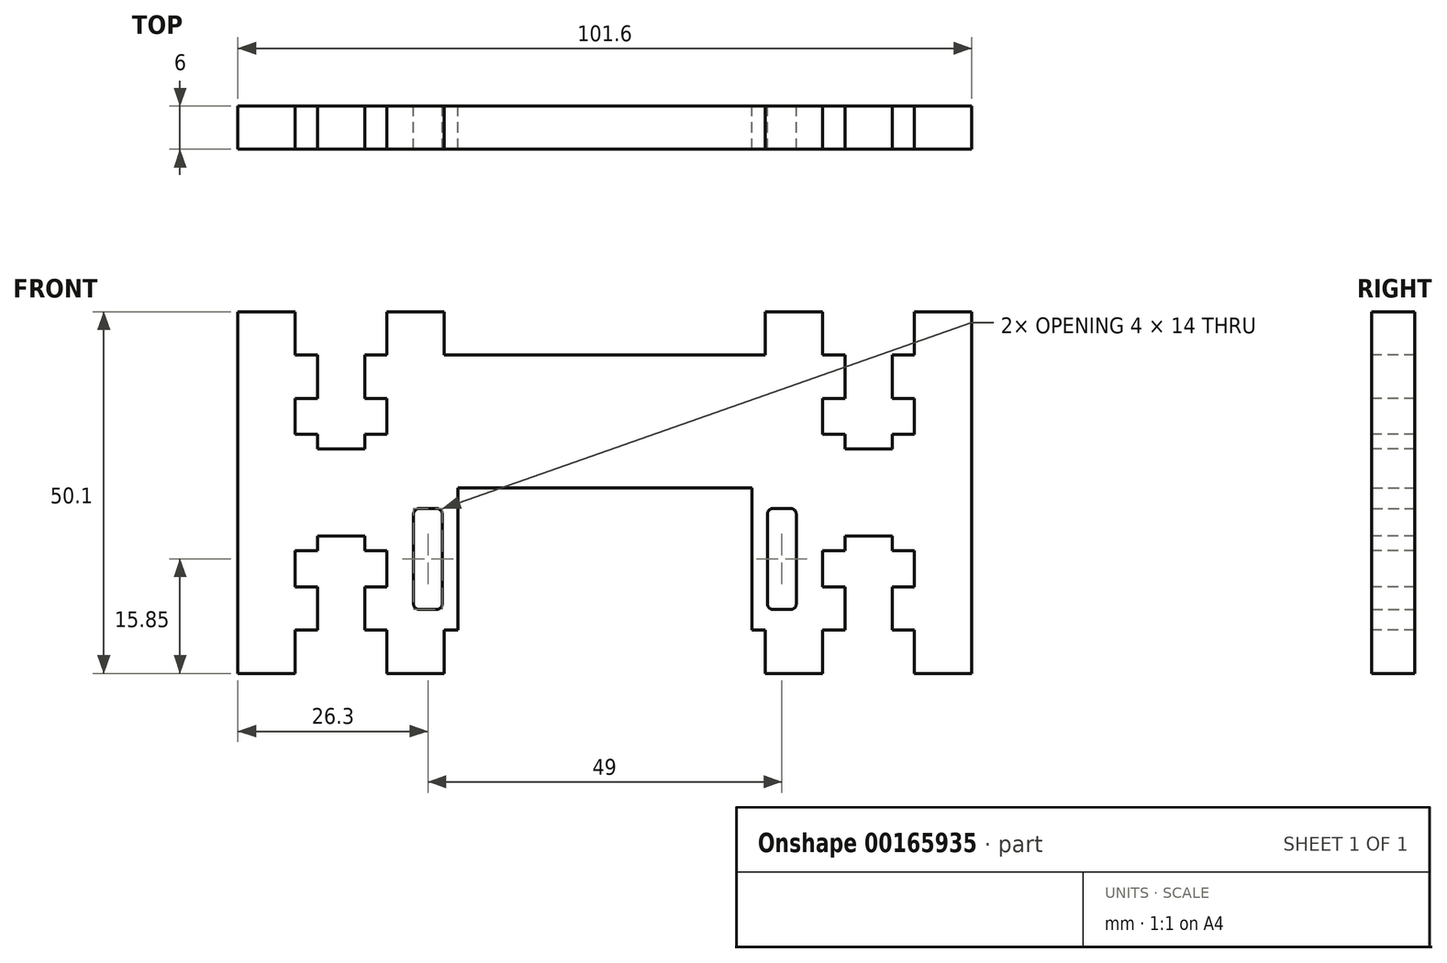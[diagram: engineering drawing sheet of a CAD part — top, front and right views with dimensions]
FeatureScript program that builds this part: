
annotation { "Feature Type Name" : "Feature", "Feature Type Description" : "" }
export const myFeature = defineFeature(function(context is Context, id is Id, definition is map)
    precondition{}
    {
        {
            var Q0;
            Q0=qCreatedBy(makeId("Front.planeOp"),FACE);
            var sketch = newSketch(context, id + "F0", { "sketchPlane" : qUnion([Q0])});
            skLineSegment(sketch, "E0.bottom", {"start": v(-50.8, 38.1) * mm, "end": v(50.8, 38.1) * mm});
            skLineSegment(sketch, "E0.top", {"start": v(-50.8, 0) * mm, "end": v(50.8, 0) * mm});
            skLineSegment(sketch, "E0.left", {"start": v(-50.8, 38.1) * mm, "end": v(-50.8, 0) * mm});
            skLineSegment(sketch, "E0.right", {"start": v(50.8, 38.1) * mm, "end": v(50.8, 0) * mm});
            skPoint(sketch, "E1", {"position": v(0, 0) * mm});
            skLineSegment(sketch, "E2.bottom", {"start": v(-20.35, 0) * mm, "end": v(20.35, 0) * mm});
            skLineSegment(sketch, "E2.top", {"start": v(-20.35, 19.7) * mm, "end": v(20.35, 19.7) * mm});
            skLineSegment(sketch, "E2.left", {"start": v(-20.35, 0) * mm, "end": v(-20.35, 19.7) * mm});
            skLineSegment(sketch, "E2.right", {"start": v(20.35, 0) * mm, "end": v(20.35, 19.7) * mm});
            skPoint(sketch, "E3", {"position": v(0, 19.7) * mm});
            skLineSegment(sketch, "E4.bottom", {"start": v(22.5, 16.85) * mm, "end": v(26.5, 16.85) * mm});
            skLineSegment(sketch, "E4.top", {"start": v(22.5, 2.85) * mm, "end": v(26.5, 2.85) * mm});
            skLineSegment(sketch, "E4.left", {"start": v(22.5, 16.85) * mm, "end": v(22.5, 2.85) * mm});
            skLineSegment(sketch, "E4.right", {"start": v(26.5, 16.85) * mm, "end": v(26.5, 2.85) * mm});
            skLineSegment(sketch, "E5", {"start": v(-20.35, 9.85) * mm, "end": v(36.92, 9.85) * mm, "construction": true});
            skPoint(sketch, "E6", {"position": v(26.5, 9.85) * mm});
            skLineSegment(sketch, "E7", {"start": v(24.5, 16.85) * mm, "end": v(24.5, 2.85) * mm, "construction": true});
            skLineSegment(sketch, "E8.MirrorCS", {"start": v(-22.5, 16.85) * mm, "end": v(-22.5, 2.85) * mm});
            skLineSegment(sketch, "E9.MirrorCS", {"start": v(-26.5, 16.85) * mm, "end": v(-26.5, 2.85) * mm});
            skLineSegment(sketch, "E10.MirrorCS", {"start": v(-22.5, 16.85) * mm, "end": v(-26.5, 16.85) * mm});
            skLineSegment(sketch, "E11.MirrorCS", {"start": v(-22.5, 2.85) * mm, "end": v(-26.5, 2.85) * mm});
            skSolve(sketch);
        }
        {
            var Q0;
            Q0=makeQuery(id+"F0.imprint","IMPRINT",FACE,{"disambiguationData":[TD([[makeQuery(id+"F0.imprint","IMPRINT",EDGE,{"derivedFrom":sQuery(id+"F0.wireOp",EDGE,"E0.bottom")}),-1.0]])]});
            extrude(context, id + "F1", {"entities" : qUnion([Q0]), "depth" : 6 * mm});
        }
        {
            var Q0;
            Q0=makeQuery(id+"F1.opExtrude","SWEPT_EDGE",EDGE,{"disambiguationData":[OSD([sQuery(id+"F0.wireOp",EDGE,"E9.MirrorCS"),sQuery(id+"F0.wireOp",EDGE,"E10.MirrorCS")])]});
            var Q1;
            Q1=makeQuery(id+"F1.opExtrude","SWEPT_EDGE",EDGE,{"disambiguationData":[OSD([sQuery(id+"F0.wireOp",EDGE,"E8.MirrorCS"),sQuery(id+"F0.wireOp",EDGE,"E11.MirrorCS")])]});
            var Q2;
            Q2=makeQuery(id+"F1.opExtrude","SWEPT_EDGE",EDGE,{"disambiguationData":[OSD([sQuery(id+"F0.wireOp",EDGE,"E8.MirrorCS"),sQuery(id+"F0.wireOp",EDGE,"E10.MirrorCS")])]});
            var Q3;
            Q3=makeQuery(id+"F1.opExtrude","SWEPT_EDGE",EDGE,{"disambiguationData":[OSD([sQuery(id+"F0.wireOp",EDGE,"E9.MirrorCS"),sQuery(id+"F0.wireOp",EDGE,"E11.MirrorCS")])]});
            var Q4;
            Q4=makeQuery(id+"F1.opExtrude","SWEPT_EDGE",EDGE,{"disambiguationData":[OSD([sQuery(id+"F0.wireOp",EDGE,"E4.top"),sQuery(id+"F0.wireOp",EDGE,"E4.left")])]});
            var Q5;
            Q5=makeQuery(id+"F1.opExtrude","SWEPT_EDGE",EDGE,{"disambiguationData":[OSD([sQuery(id+"F0.wireOp",EDGE,"E4.bottom"),sQuery(id+"F0.wireOp",EDGE,"E4.left")])]});
            var Q6;
            Q6=makeQuery(id+"F1.opExtrude","SWEPT_EDGE",EDGE,{"disambiguationData":[OSD([sQuery(id+"F0.wireOp",EDGE,"E4.bottom"),sQuery(id+"F0.wireOp",EDGE,"E4.right")])]});
            var Q7;
            Q7=makeQuery(id+"F1.opExtrude","SWEPT_EDGE",EDGE,{"disambiguationData":[OSD([sQuery(id+"F0.wireOp",EDGE,"E4.top"),sQuery(id+"F0.wireOp",EDGE,"E4.right")])]});
            fillet(context, id + "F2", {"entities" : qUnion([Q0, Q1, Q2, Q3, Q4, Q5, Q6, Q7]), "radius" : .8 * mm, "tangentPropagation" : true, "allowEdgeOverflow" : false});
        }
        {
            var Q0;
            {var subQ0=sQuery(id+"F0.wireOp",EDGE,"E0.top");Q0=makeQuery(id+"F1.opExtrude","SWEPT_FACE",FACE,{"disambiguationData":[OSD([subQ0]),TDD([makeQuery(id+"F0.imprint","IMPRINT",EDGE,{"disambiguationData":[TD([[makeQuery(id+"F0.imprint","INTERSECT",VERTEX,{"derivedFrom":[subQ0,sQuery(id+"F0.wireOp",EDGE,"E0.left")]}),-1.0]])],"derivedFrom":subQ0})])]});}
            var sketch = newSketch(context, id + "F3", { "sketchPlane" : qUnion([Q0])});
            skLineSegment(sketch, "E12.bottom", {"start": v(-50.8, 6) * mm, "end": v(-42.86, 6) * mm});
            skLineSegment(sketch, "E12.top", {"start": v(-50.8, 0) * mm, "end": v(-42.86, 0) * mm});
            skLineSegment(sketch, "E12.left", {"start": v(-50.8, 6) * mm, "end": v(-50.8, 0) * mm});
            skLineSegment(sketch, "E12.right", {"start": v(-42.86, 6) * mm, "end": v(-42.86, 0) * mm});
            skLineSegment(sketch, "E13.MirrorCS", {"start": v(50.8, 0) * mm, "end": v(42.86, 0) * mm});
            skLineSegment(sketch, "E14.MirrorCS", {"start": v(42.86, 6) * mm, "end": v(42.86, 0) * mm});
            skLineSegment(sketch, "E15.MirrorCS", {"start": v(50.8, 6) * mm, "end": v(42.86, 6) * mm});
            skLineSegment(sketch, "E16.MirrorCS", {"start": v(50.8, 6) * mm, "end": v(50.8, 0) * mm});
            skLineSegment(sketch, "E17.bottom", {"start": v(-30.16, 6) * mm, "end": v(-22.23, 6) * mm});
            skLineSegment(sketch, "E17.top", {"start": v(-30.16, 0) * mm, "end": v(-22.23, 0) * mm});
            skLineSegment(sketch, "E17.left", {"start": v(-30.16, 6) * mm, "end": v(-30.16, 0) * mm});
            skLineSegment(sketch, "E17.right", {"start": v(-22.23, 6) * mm, "end": v(-22.23, 0) * mm});
            skLineSegment(sketch, "E18.bottom", {"start": v(30.16, 6) * mm, "end": v(22.23, 6) * mm});
            skLineSegment(sketch, "E18.top", {"start": v(30.16, 0) * mm, "end": v(22.23, 0) * mm});
            skLineSegment(sketch, "E18.left", {"start": v(30.16, 6) * mm, "end": v(30.16, 0) * mm});
            skLineSegment(sketch, "E18.right", {"start": v(22.23, 6) * mm, "end": v(22.23, 0) * mm});
            skSolve(sketch);
        }
        {
            var Q0;
            Q0=qSketchRegion(id+"F3",true);
            extrude(context, id + "F4", {"entities" : qUnion([Q0]), "operationType" : NewBodyOperationType.ADD, "depth" : 6 * mm});
        }
        {
            var Q0;
            Q0=makeQuery(id+"F1.opExtrude","SWEPT_FACE",FACE,{"disambiguationData":[OSD([sQuery(id+"F0.wireOp",EDGE,"E0.bottom")])]});
            var sketch = newSketch(context, id + "F5", { "sketchPlane" : qUnion([Q0])});
            skLineSegment(sketch, "E19.bottom", {"start": v(-50.8, 0) * mm, "end": v(-42.86, 0) * mm});
            skLineSegment(sketch, "E19.top", {"start": v(-50.8, -6) * mm, "end": v(-42.86, -6) * mm});
            skLineSegment(sketch, "E19.left", {"start": v(-50.8, 0) * mm, "end": v(-50.8, -6) * mm});
            skLineSegment(sketch, "E19.right", {"start": v(-42.86, 0) * mm, "end": v(-42.86, -6) * mm});
            skLineSegment(sketch, "E20.bottom", {"start": v(-30.16, 0) * mm, "end": v(-22.22, 0) * mm});
            skLineSegment(sketch, "E20.top", {"start": v(-30.16, -6) * mm, "end": v(-22.22, -6) * mm});
            skLineSegment(sketch, "E20.left", {"start": v(-30.16, 0) * mm, "end": v(-30.16, -6) * mm});
            skLineSegment(sketch, "E20.right", {"start": v(-22.22, 0) * mm, "end": v(-22.22, -6) * mm});
            skLineSegment(sketch, "E21.bottom", {"start": v(22.23, 0) * mm, "end": v(30.16, 0) * mm});
            skLineSegment(sketch, "E21.top", {"start": v(22.23, -6) * mm, "end": v(30.16, -6) * mm});
            skLineSegment(sketch, "E21.left", {"start": v(22.23, 0) * mm, "end": v(22.23, -6) * mm});
            skLineSegment(sketch, "E21.right", {"start": v(30.16, 0) * mm, "end": v(30.16, -6) * mm});
            skLineSegment(sketch, "E22.bottom", {"start": v(42.86, 0) * mm, "end": v(50.8, 0) * mm});
            skLineSegment(sketch, "E22.top", {"start": v(42.86, -6) * mm, "end": v(50.8, -6) * mm});
            skLineSegment(sketch, "E22.left", {"start": v(42.86, 0) * mm, "end": v(42.86, -6) * mm});
            skLineSegment(sketch, "E22.right", {"start": v(50.8, 0) * mm, "end": v(50.8, -6) * mm});
            skSolve(sketch);
        }
        {
            var Q0;
            Q0=qSketchRegion(id+"F5",true);
            extrude(context, id + "F6", {"entities" : qUnion([Q0]), "operationType" : NewBodyOperationType.ADD, "depth" : 6 * mm});
        }
        {
            var Q0;
            Q0=makeQuery(id+"F6.boolean.opBoolean","MERGE",FACE,{"derivedFrom":[makeQuery(id+"F4.boolean.opBoolean","MERGE",FACE,{"derivedFrom":[makeQuery(id+"F1.opExtrude","CAP_FACE",FACE,{"disambiguationData":[OSD([sQuery(id+"F0.wireOp",EDGE,"E0.bottom"),sQuery(id+"F0.wireOp",EDGE,"E0.top"),sQuery(id+"F0.wireOp",EDGE,"E0.left"),sQuery(id+"F0.wireOp",EDGE,"E0.right"),sQuery(id+"F0.wireOp",EDGE,"E2.top"),sQuery(id+"F0.wireOp",EDGE,"E2.left"),sQuery(id+"F0.wireOp",EDGE,"E2.right"),sQuery(id+"F0.wireOp",EDGE,"E4.bottom"),sQuery(id+"F0.wireOp",EDGE,"E4.top"),sQuery(id+"F0.wireOp",EDGE,"E4.left"),sQuery(id+"F0.wireOp",EDGE,"E4.right"),sQuery(id+"F0.wireOp",EDGE,"E8.MirrorCS"),sQuery(id+"F0.wireOp",EDGE,"E9.MirrorCS"),sQuery(id+"F0.wireOp",EDGE,"E10.MirrorCS"),sQuery(id+"F0.wireOp",EDGE,"E11.MirrorCS")])],"isStart":false}),makeQuery(id+"F4.opExtrude","SWEPT_FACE",FACE,{"disambiguationData":[OSD([sQuery(id+"F3.wireOp",EDGE,"E12.bottom")])]}),makeQuery(id+"F4.opExtrude","SWEPT_FACE",FACE,{"disambiguationData":[OSD([sQuery(id+"F3.wireOp",EDGE,"E15.MirrorCS")])]}),makeQuery(id+"F4.opExtrude","SWEPT_FACE",FACE,{"disambiguationData":[OSD([sQuery(id+"F3.wireOp",EDGE,"E17.bottom")])]}),makeQuery(id+"F4.opExtrude","SWEPT_FACE",FACE,{"disambiguationData":[OSD([sQuery(id+"F3.wireOp",EDGE,"E18.bottom")])]})]}),makeQuery(id+"F6.opExtrude","SWEPT_FACE",FACE,{"disambiguationData":[OSD([sQuery(id+"F5.wireOp",EDGE,"E19.top")])]}),makeQuery(id+"F6.opExtrude","SWEPT_FACE",FACE,{"disambiguationData":[OSD([sQuery(id+"F5.wireOp",EDGE,"E20.top")])]}),makeQuery(id+"F6.opExtrude","SWEPT_FACE",FACE,{"disambiguationData":[OSD([sQuery(id+"F5.wireOp",EDGE,"E21.top")])]}),makeQuery(id+"F6.opExtrude","SWEPT_FACE",FACE,{"disambiguationData":[OSD([sQuery(id+"F5.wireOp",EDGE,"E22.top")])]})]});
            var sketch = newSketch(context, id + "F7", { "sketchPlane" : qUnion([Q0])});
            skLineSegment(sketch, "E23", {"start": v(0, 38.1) * mm, "end": v(0, 19.7) * mm, "construction": true});
            skLineSegment(sketch, "E24", {"start": v(-50.8, 19.05) * mm, "end": v(50.8, 19.05) * mm, "construction": true});
            skLineSegment(sketch, "E25", {"start": v(-36.51, 38.1) * mm, "end": v(-39.76, 38.1) * mm});
            skLineSegment(sketch, "E26", {"start": v(-39.76, 38.1) * mm, "end": v(-39.76, 32.1) * mm});
            skLineSegment(sketch, "E27", {"start": v(-39.76, 32.1) * mm, "end": v(-42.86, 32.1) * mm});
            skLineSegment(sketch, "E28", {"start": v(-42.86, 32.1) * mm, "end": v(-42.86, 27.1) * mm});
            skLineSegment(sketch, "E29", {"start": v(-42.86, 27.1) * mm, "end": v(-39.76, 27.1) * mm});
            skLineSegment(sketch, "E30", {"start": v(-39.76, 27.1) * mm, "end": v(-39.76, 25.1) * mm});
            skLineSegment(sketch, "E31", {"start": v(-39.76, 25.1) * mm, "end": v(-36.51, 25.1) * mm});
            skLineSegment(sketch, "E32", {"start": v(-36.51, 38.1) * mm, "end": v(-36.51, 25.1) * mm, "construction": true});
            skLineSegment(sketch, "E33.MirrorCS", {"start": v(-36.51, 38.1) * mm, "end": v(-33.26, 38.1) * mm});
            skLineSegment(sketch, "E34.MirrorCS", {"start": v(-33.26, 38.1) * mm, "end": v(-33.26, 32.1) * mm});
            skLineSegment(sketch, "E35.MirrorCS", {"start": v(-33.26, 32.1) * mm, "end": v(-30.16, 32.1) * mm});
            skLineSegment(sketch, "E36.MirrorCS", {"start": v(-30.16, 32.1) * mm, "end": v(-30.16, 27.1) * mm});
            skLineSegment(sketch, "E37.MirrorCS", {"start": v(-30.16, 27.1) * mm, "end": v(-33.26, 27.1) * mm});
            skLineSegment(sketch, "E38.MirrorCS", {"start": v(-33.26, 27.1) * mm, "end": v(-33.26, 25.1) * mm});
            skLineSegment(sketch, "E39.MirrorCS", {"start": v(-33.26, 25.1) * mm, "end": v(-36.51, 25.1) * mm});
            skLineSegment(sketch, "E40.MirrorCS", {"start": v(39.76, 38.1) * mm, "end": v(39.76, 32.1) * mm});
            skLineSegment(sketch, "E41.MirrorCS", {"start": v(33.26, 38.1) * mm, "end": v(33.26, 32.1) * mm});
            skLineSegment(sketch, "E42.MirrorCS", {"start": v(33.26, 32.1) * mm, "end": v(30.16, 32.1) * mm});
            skLineSegment(sketch, "E43.MirrorCS", {"start": v(36.51, 38.1) * mm, "end": v(39.76, 38.1) * mm});
            skLineSegment(sketch, "E44.MirrorCS", {"start": v(36.51, 38.1) * mm, "end": v(33.26, 38.1) * mm});
            skLineSegment(sketch, "E45.MirrorCS", {"start": v(30.16, 32.1) * mm, "end": v(30.16, 27.1) * mm});
            skLineSegment(sketch, "E46.MirrorCS", {"start": v(30.16, 27.1) * mm, "end": v(33.26, 27.1) * mm});
            skLineSegment(sketch, "E47.MirrorCS", {"start": v(33.26, 27.1) * mm, "end": v(33.26, 25.1) * mm});
            skLineSegment(sketch, "E48.MirrorCS", {"start": v(33.26, 25.1) * mm, "end": v(36.51, 25.1) * mm});
            skLineSegment(sketch, "E49.MirrorCS", {"start": v(39.76, 25.1) * mm, "end": v(36.51, 25.1) * mm});
            skLineSegment(sketch, "E50.MirrorCS", {"start": v(39.76, 27.1) * mm, "end": v(39.76, 25.1) * mm});
            skLineSegment(sketch, "E51.MirrorCS", {"start": v(42.86, 27.1) * mm, "end": v(39.76, 27.1) * mm});
            skLineSegment(sketch, "E52.MirrorCS", {"start": v(42.86, 32.1) * mm, "end": v(42.86, 27.1) * mm});
            skLineSegment(sketch, "E53.MirrorCS", {"start": v(39.76, 32.1) * mm, "end": v(42.86, 32.1) * mm});
            skLineSegment(sketch, "E54.MirrorCS", {"start": v(33.26, 0) * mm, "end": v(33.26, 6) * mm});
            skLineSegment(sketch, "E55.MirrorCS", {"start": v(33.26, 6) * mm, "end": v(30.16, 6) * mm});
            skLineSegment(sketch, "E56.MirrorCS", {"start": v(30.16, 6) * mm, "end": v(30.16, 11) * mm});
            skLineSegment(sketch, "E57.MirrorCS", {"start": v(30.16, 11) * mm, "end": v(33.26, 11) * mm});
            skLineSegment(sketch, "E58.MirrorCS", {"start": v(33.26, 11) * mm, "end": v(33.26, 13) * mm});
            skLineSegment(sketch, "E59.MirrorCS", {"start": v(33.26, 13) * mm, "end": v(36.51, 13) * mm});
            skLineSegment(sketch, "E60.MirrorCS", {"start": v(39.76, 13) * mm, "end": v(36.51, 13) * mm});
            skLineSegment(sketch, "E61.MirrorCS", {"start": v(39.76, 11) * mm, "end": v(39.76, 13) * mm});
            skLineSegment(sketch, "E62.MirrorCS", {"start": v(42.86, 11) * mm, "end": v(39.76, 11) * mm});
            skLineSegment(sketch, "E63.MirrorCS", {"start": v(42.86, 6) * mm, "end": v(42.86, 11) * mm});
            skLineSegment(sketch, "E64.MirrorCS", {"start": v(39.76, 6) * mm, "end": v(42.86, 6) * mm});
            skLineSegment(sketch, "E65.MirrorCS", {"start": v(39.76, 0) * mm, "end": v(39.76, 6) * mm});
            skLineSegment(sketch, "E66.MirrorCS", {"start": v(36.51, 0) * mm, "end": v(39.76, 0) * mm});
            skLineSegment(sketch, "E67.MirrorCS", {"start": v(36.51, 0) * mm, "end": v(33.26, 0) * mm});
            skLineSegment(sketch, "E68.MirrorCS", {"start": v(-39.76, 0) * mm, "end": v(-39.76, 6) * mm});
            skLineSegment(sketch, "E69.MirrorCS", {"start": v(-36.51, 0) * mm, "end": v(-39.76, 0) * mm});
            skLineSegment(sketch, "E70.MirrorCS", {"start": v(-36.51, 0) * mm, "end": v(-33.26, 0) * mm});
            skLineSegment(sketch, "E71.MirrorCS", {"start": v(-33.26, 0) * mm, "end": v(-33.26, 6) * mm});
            skLineSegment(sketch, "E72.MirrorCS", {"start": v(-33.26, 6) * mm, "end": v(-30.16, 6) * mm});
            skLineSegment(sketch, "E73.MirrorCS", {"start": v(-30.16, 6) * mm, "end": v(-30.16, 11) * mm});
            skLineSegment(sketch, "E74.MirrorCS", {"start": v(-30.16, 11) * mm, "end": v(-33.26, 11) * mm});
            skLineSegment(sketch, "E75.MirrorCS", {"start": v(-33.26, 13) * mm, "end": v(-36.51, 13) * mm});
            skLineSegment(sketch, "E76.MirrorCS", {"start": v(-39.76, 13) * mm, "end": v(-36.51, 13) * mm});
            skLineSegment(sketch, "E77.MirrorCS", {"start": v(-39.76, 11) * mm, "end": v(-39.76, 13) * mm});
            skLineSegment(sketch, "E78.MirrorCS", {"start": v(-42.86, 11) * mm, "end": v(-39.76, 11) * mm});
            skLineSegment(sketch, "E79.MirrorCS", {"start": v(-42.86, 6) * mm, "end": v(-42.86, 11) * mm});
            skLineSegment(sketch, "E80.MirrorCS", {"start": v(-39.76, 6) * mm, "end": v(-42.86, 6) * mm});
            skLineSegment(sketch, "E81.MirrorCS", {"start": v(-33.26, 11) * mm, "end": v(-33.26, 13) * mm});
            skSolve(sketch);
        }
        {
            var Q0;
            Q0=qSketchRegion(id+"F7",true);
            extrude(context, id + "F8", {"entities" : qUnion([Q0]), "operationType" : NewBodyOperationType.REMOVE, "oppositeDirection" : true, "depth" : 25.4 * mm});
        }
    });
